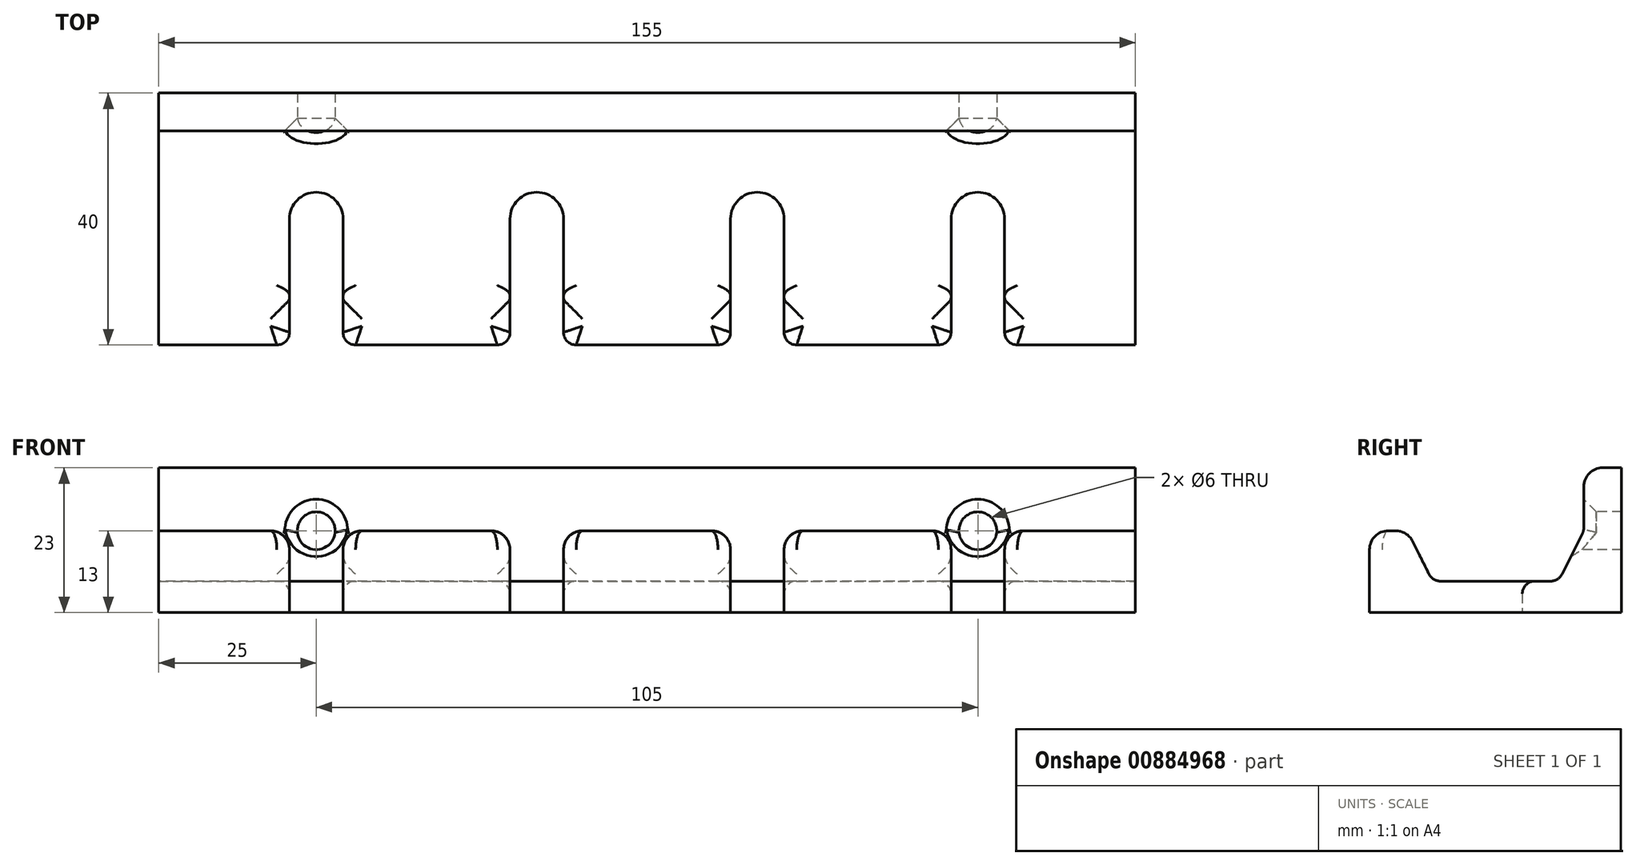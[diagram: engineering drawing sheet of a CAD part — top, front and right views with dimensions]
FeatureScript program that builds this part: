
annotation { "Feature Type Name" : "Feature", "Feature Type Description" : "" }
export const myFeature = defineFeature(function(context is Context, id is Id, definition is map)
    precondition{}
    {
        {
            var Q0;
            Q0=qCreatedBy(makeId("Top.planeOp"),FACE);
            var sketch = newSketch(context, id + "F0", { "sketchPlane" : qUnion([Q0])});
            skLineSegment(sketch, "E0.bottom", {"start": v(-77.5, 20) * mm, "end": v(77.5, 20) * mm});
            skLineSegment(sketch, "E0.top", {"start": v(-77.5, -20) * mm, "end": v(77.5, -20) * mm});
            skLineSegment(sketch, "E0.left", {"start": v(-77.5, 20) * mm, "end": v(-77.5, -20) * mm});
            skLineSegment(sketch, "E0.right", {"start": v(77.5, 20) * mm, "end": v(77.5, -20) * mm});
            skPoint(sketch, "E0.middle", {"position": v(0, 0) * mm});
            skSolve(sketch);
        }
        {
            var Q0;
            Q0=makeQuery(id+"F0.imprint","IMPRINT",FACE,{"disambiguationData":[TD([[makeQuery(id+"F0.imprint","IMPRINT",EDGE,{"derivedFrom":sQuery(id+"F0.wireOp",EDGE,"E0.bottom")}),-1.0]])]});
            extrude(context, id + "F1", {"entities" : qUnion([Q0]), "depth" : 5 * mm, "offsetDistance" : 25 * mm});
        }
        {
            var Q0;
            Q0=makeQuery(id+"F1.opExtrude","CAP_FACE",FACE,{"disambiguationData":[OSD([sQuery(id+"F0.wireOp",EDGE,"E0.bottom"),sQuery(id+"F0.wireOp",EDGE,"E0.top"),sQuery(id+"F0.wireOp",EDGE,"E0.left"),sQuery(id+"F0.wireOp",EDGE,"E0.right")])],"isStart":false});
            var sketch = newSketch(context, id + "F2", { "sketchPlane" : qUnion([Q0])});
            skLineSegment(sketch, "E1.bottom", {"start": v(-77.5, 10) * mm, "end": v(77.5, 10) * mm});
            skLineSegment(sketch, "E1.top", {"start": v(-77.5, -10) * mm, "end": v(77.5, -10) * mm});
            skLineSegment(sketch, "E1.left", {"start": v(-77.5, 10) * mm, "end": v(-77.5, -10) * mm});
            skLineSegment(sketch, "E1.right", {"start": v(77.5, 10) * mm, "end": v(77.5, -10) * mm});
            skPoint(sketch, "E1.middle", {"position": v(0, 0) * mm});
            skLineSegment(sketch, "E2.bottom", {"start": v(-77.5, 20) * mm, "end": v(77.5, 20) * mm});
            skLineSegment(sketch, "E2.top", {"start": v(-77.5, -20) * mm, "end": v(77.5, -20) * mm});
            skLineSegment(sketch, "E2.left", {"start": v(-77.5, 20) * mm, "end": v(-77.5, -20) * mm});
            skLineSegment(sketch, "E2.right", {"start": v(77.5, 20) * mm, "end": v(77.5, -20) * mm});
            skSolve(sketch);
        }
        {
            var Q0;
            {var subQ0=sQuery(id+"F2.wireOp",EDGE,"E1.bottom");Q0=makeQuery(id+"F2.imprint","IMPRINT",FACE,{"disambiguationData":[TD([[makeQuery(id+"F2.imprint","IMPRINT",EDGE,{"derivedFrom":subQ0}),1.0]])]});}
            var Q1;
            {var subQ0=sQuery(id+"F2.wireOp",EDGE,"E1.top");Q1=makeQuery(id+"F2.imprint","IMPRINT",FACE,{"disambiguationData":[TD([[makeQuery(id+"F2.imprint","IMPRINT",EDGE,{"derivedFrom":subQ0}),-1.0]])]});}
            extrude(context, id + "F3", {"entities" : qUnion([Q0, Q1]), "operationType" : NewBodyOperationType.ADD, "depth" : 8 * mm, "offsetDistance" : 25 * mm});
        }
        {
            var Q0;
            Q0=makeQuery(id+"F3.opExtrude","CAP_EDGE",EDGE,{"disambiguationData":[OSD([sQuery(id+"F2.wireOp",EDGE,"E1.bottom")])],"isStart":false});
            chamfer(context, id + "F4", {"entities" : qUnion([Q0]), "chamferType" : ChamferType.TWO_OFFSETS, "width1" : 8 * mm, "oppositeDirection" : true, "width2" : 4 * mm});
        }
        {
            var Q0;
            Q0=makeQuery(id+"F3.opExtrude","CAP_EDGE",EDGE,{"disambiguationData":[OSD([sQuery(id+"F2.wireOp",EDGE,"E1.top")])],"isStart":false});
            chamfer(context, id + "F5", {"entities" : qUnion([Q0]), "chamferType" : ChamferType.TWO_OFFSETS, "width1" : 8 * mm, "oppositeDirection" : false, "width2" : 4 * mm, "tangentPropagation" : true});
        }
        {
            var Q0;
            Q0=makeQuery(id+"F0.imprint","IMPRINT",FACE,{"disambiguationData":[TD([[makeQuery(id+"F0.imprint","IMPRINT",EDGE,{"derivedFrom":sQuery(id+"F0.wireOp",EDGE,"E0.bottom")}),-1.0]])]});
            var sketch = newSketch(context, id + "F6", { "sketchPlane" : qUnion([Q0])});
            skCircle(sketch, "E3", {"center": v(-52.5, 0) * mm, "radius": 4.25 * mm});
            skCircle(sketch, "E4.1.0.0", {"center": v(-17.5, 0) * mm, "radius": 4.25 * mm});
            skCircle(sketch, "E4.2.0.0", {"center": v(17.5, 0) * mm, "radius": 4.25 * mm});
            skCircle(sketch, "E4.3.0.0", {"center": v(52.5, 0) * mm, "radius": 4.25 * mm});
            skLineSegment(sketch, "E4.direction1", {"start": v(-52.5, 0) * mm, "end": v(-17.5, 0) * mm, "construction": true});
            skLineSegment(sketch, "E5", {"start": v(-48.25, 0) * mm, "end": v(-48.25, -25) * mm});
            skLineSegment(sketch, "E6", {"start": v(-56.75, 0) * mm, "end": v(-56.75, -25) * mm});
            skLineSegment(sketch, "E7", {"start": v(-21.75, 0) * mm, "end": v(-21.75, -25) * mm});
            skLineSegment(sketch, "E8", {"start": v(-80.14, 0) * mm, "end": v(82.26, 0) * mm, "construction": true});
            skLineSegment(sketch, "E9", {"start": v(-13.25, 0) * mm, "end": v(-13.25, -25) * mm});
            skLineSegment(sketch, "E10", {"start": v(13.25, 0) * mm, "end": v(13.25, -25) * mm});
            skLineSegment(sketch, "E11", {"start": v(21.75, 0) * mm, "end": v(21.75, -25) * mm});
            skLineSegment(sketch, "E12", {"start": v(48.25, 0) * mm, "end": v(48.25, -25) * mm});
            skLineSegment(sketch, "E13", {"start": v(56.75, 0) * mm, "end": v(56.75, -25) * mm});
            skLineSegment(sketch, "E14", {"start": v(-48.25, -25) * mm, "end": v(-56.75, -25) * mm});
            skLineSegment(sketch, "E15", {"start": v(-21.75, -25) * mm, "end": v(-13.25, -25) * mm});
            skLineSegment(sketch, "E16", {"start": v(13.25, -25) * mm, "end": v(21.75, -25) * mm});
            skLineSegment(sketch, "E17", {"start": v(48.25, -25) * mm, "end": v(56.75, -25) * mm});
            skSolve(sketch);
        }
        {
            var Q0;
            Q0 = qSketchRegion(id + "F6", true);
            extrude(context, id + "F7", {"entities" : qUnion([Q0]), "operationType" : NewBodyOperationType.REMOVE, "depth" : 25 * mm, "offsetDistance" : 25 * mm});
        }
        {
            var Q0;
            Q0=makeQuery(id+"F3.opExtrude","CAP_FACE",FACE,{"disambiguationData":[OSD([sQuery(id+"F2.wireOp",EDGE,"E1.bottom"),sQuery(id+"F2.wireOp",EDGE,"E2.bottom"),sQuery(id+"F2.wireOp",EDGE,"E2.left"),sQuery(id+"F2.wireOp",EDGE,"E2.right")])],"isStart":false});
            extrude(context, id + "F8", {"entities" : qUnion([Q0]), "operationType" : NewBodyOperationType.ADD, "depth" : 10 * mm, "offsetDistance" : 25 * mm});
        }
        {
            var Q0;
            Q0=makeQuery(id+"F8.opExtrude","SWEPT_FACE",FACE,{"disambiguationData":[OSD([sQuery(id+"F2.wireOp",EDGE,"E1.bottom"),sQuery(id+"F2.wireOp",EDGE,"E2.bottom"),sQuery(id+"F2.wireOp",EDGE,"E2.left"),sQuery(id+"F2.wireOp",EDGE,"E2.right")])]});
            var sketch = newSketch(context, id + "F9", { "sketchPlane" : qUnion([Q0])});
            skCircle(sketch, "E18", {"center": v(-52.5, 13) * mm, "radius": 3 * mm});
            skCircle(sketch, "E19", {"center": v(52.5, 13) * mm, "radius": 3 * mm});
            skSolve(sketch);
        }
        {
            var Q0;
            Q0 = qSketchRegion(id + "F9", true);
            extrude(context, id + "F10", {"entities" : qUnion([Q0]), "operationType" : NewBodyOperationType.REMOVE, "oppositeDirection" : true, "depth" : 15 * mm, "offsetDistance" : 25 * mm, "hasSecondDirection" : true, "secondDirectionOppositeDirection" : false, "secondDirectionDepth" : 15 * mm});
        }
        {
            var Q0;
            Q0=makeQuery(id+"F10.boolean.opBoolean","INTERSECT",EDGE,{"derivedFrom":[makeQuery(id+"F4.opChamfer","BLEND_FACE",FACE,{"disambiguationData":[OSD([sQuery(id+"F2.wireOp",EDGE,"E1.bottom")])]}),makeQuery(id+"F10.opExtrude","SWEPT_FACE",FACE,{"disambiguationData":[OSD([sQuery(id+"F9.wireOp",EDGE,"E18")])]})]});
            var Q1;
            Q1=makeQuery(id+"F10.boolean.opBoolean","INTERSECT",EDGE,{"derivedFrom":[makeQuery(id+"F8.opExtrude","SWEPT_FACE",FACE,{"disambiguationData":[OSD([sQuery(id+"F2.wireOp",EDGE,"E1.bottom"),sQuery(id+"F2.wireOp",EDGE,"E2.bottom"),sQuery(id+"F2.wireOp",EDGE,"E2.left"),sQuery(id+"F2.wireOp",EDGE,"E2.right")])]}),makeQuery(id+"F10.opExtrude","SWEPT_FACE",FACE,{"disambiguationData":[OSD([sQuery(id+"F9.wireOp",EDGE,"E18")])]})]});
            var Q2;
            Q2=makeQuery(id+"F10.boolean.opBoolean","INTERSECT",EDGE,{"derivedFrom":[makeQuery(id+"F4.opChamfer","BLEND_FACE",FACE,{"disambiguationData":[OSD([sQuery(id+"F2.wireOp",EDGE,"E1.bottom")])]}),makeQuery(id+"F10.opExtrude","SWEPT_FACE",FACE,{"disambiguationData":[OSD([sQuery(id+"F9.wireOp",EDGE,"E19")])]})]});
            var Q3;
            Q3=makeQuery(id+"F10.boolean.opBoolean","INTERSECT",EDGE,{"derivedFrom":[makeQuery(id+"F8.opExtrude","SWEPT_FACE",FACE,{"disambiguationData":[OSD([sQuery(id+"F2.wireOp",EDGE,"E1.bottom"),sQuery(id+"F2.wireOp",EDGE,"E2.bottom"),sQuery(id+"F2.wireOp",EDGE,"E2.left"),sQuery(id+"F2.wireOp",EDGE,"E2.right")])]}),makeQuery(id+"F10.opExtrude","SWEPT_FACE",FACE,{"disambiguationData":[OSD([sQuery(id+"F9.wireOp",EDGE,"E19")])]})]});
            chamfer(context, id + "F11", {"entities" : qUnion([Q0, Q1, Q2, Q3]), "width" : 2 * mm, "tangentPropagation" : true});
        }
        {
            var Q0;
            Q0=makeQuery(id+"F7.boolean.opBoolean","INTERSECT",EDGE,{"derivedFrom":[makeQuery(id+"F1.opExtrude","CAP_FACE",FACE,{"disambiguationData":[OSD([sQuery(id+"F0.wireOp",EDGE,"E0.bottom"),sQuery(id+"F0.wireOp",EDGE,"E0.top"),sQuery(id+"F0.wireOp",EDGE,"E0.left"),sQuery(id+"F0.wireOp",EDGE,"E0.right")])],"isStart":false}),makeQuery(id+"F7.opExtrude","SWEPT_FACE",FACE,{"disambiguationData":[OSD([sQuery(id+"F6.wireOp",EDGE,"E6")])]})]});
            var Q1;
            Q1=makeQuery(id+"F7.boolean.opBoolean","INTERSECT",EDGE,{"derivedFrom":[makeQuery(id+"F1.opExtrude","CAP_FACE",FACE,{"disambiguationData":[OSD([sQuery(id+"F0.wireOp",EDGE,"E0.bottom"),sQuery(id+"F0.wireOp",EDGE,"E0.top"),sQuery(id+"F0.wireOp",EDGE,"E0.left"),sQuery(id+"F0.wireOp",EDGE,"E0.right")])],"isStart":false}),makeQuery(id+"F7.opExtrude","SWEPT_FACE",FACE,{"disambiguationData":[OSD([sQuery(id+"F6.wireOp",EDGE,"E3")])]})]});
            var Q2;
            Q2=makeQuery(id+"F7.boolean.opBoolean","INTERSECT",EDGE,{"derivedFrom":[makeQuery(id+"F1.opExtrude","CAP_FACE",FACE,{"disambiguationData":[OSD([sQuery(id+"F0.wireOp",EDGE,"E0.bottom"),sQuery(id+"F0.wireOp",EDGE,"E0.top"),sQuery(id+"F0.wireOp",EDGE,"E0.left"),sQuery(id+"F0.wireOp",EDGE,"E0.right")])],"isStart":false}),makeQuery(id+"F7.opExtrude","SWEPT_FACE",FACE,{"disambiguationData":[OSD([sQuery(id+"F6.wireOp",EDGE,"E5")])]})]});
            var Q3;
            Q3=makeQuery(id+"F7.boolean.opBoolean","INTERSECT",EDGE,{"derivedFrom":[makeQuery(id+"F1.opExtrude","CAP_FACE",FACE,{"disambiguationData":[OSD([sQuery(id+"F0.wireOp",EDGE,"E0.bottom"),sQuery(id+"F0.wireOp",EDGE,"E0.top"),sQuery(id+"F0.wireOp",EDGE,"E0.left"),sQuery(id+"F0.wireOp",EDGE,"E0.right")])],"isStart":false}),makeQuery(id+"F7.opExtrude","SWEPT_FACE",FACE,{"disambiguationData":[OSD([sQuery(id+"F6.wireOp",EDGE,"E7")])]})]});
            var Q4;
            Q4=makeQuery(id+"F7.boolean.opBoolean","INTERSECT",EDGE,{"derivedFrom":[makeQuery(id+"F1.opExtrude","CAP_FACE",FACE,{"disambiguationData":[OSD([sQuery(id+"F0.wireOp",EDGE,"E0.bottom"),sQuery(id+"F0.wireOp",EDGE,"E0.top"),sQuery(id+"F0.wireOp",EDGE,"E0.left"),sQuery(id+"F0.wireOp",EDGE,"E0.right")])],"isStart":false}),makeQuery(id+"F7.opExtrude","SWEPT_FACE",FACE,{"disambiguationData":[OSD([sQuery(id+"F6.wireOp",EDGE,"E4.1.0.0")])]})]});
            var Q5;
            Q5=makeQuery(id+"F7.boolean.opBoolean","INTERSECT",EDGE,{"derivedFrom":[makeQuery(id+"F1.opExtrude","CAP_FACE",FACE,{"disambiguationData":[OSD([sQuery(id+"F0.wireOp",EDGE,"E0.bottom"),sQuery(id+"F0.wireOp",EDGE,"E0.top"),sQuery(id+"F0.wireOp",EDGE,"E0.left"),sQuery(id+"F0.wireOp",EDGE,"E0.right")])],"isStart":false}),makeQuery(id+"F7.opExtrude","SWEPT_FACE",FACE,{"disambiguationData":[OSD([sQuery(id+"F6.wireOp",EDGE,"E9")])]})]});
            var Q6;
            Q6=makeQuery(id+"F7.boolean.opBoolean","INTERSECT",EDGE,{"derivedFrom":[makeQuery(id+"F1.opExtrude","CAP_FACE",FACE,{"disambiguationData":[OSD([sQuery(id+"F0.wireOp",EDGE,"E0.bottom"),sQuery(id+"F0.wireOp",EDGE,"E0.top"),sQuery(id+"F0.wireOp",EDGE,"E0.left"),sQuery(id+"F0.wireOp",EDGE,"E0.right")])],"isStart":false}),makeQuery(id+"F7.opExtrude","SWEPT_FACE",FACE,{"disambiguationData":[OSD([sQuery(id+"F6.wireOp",EDGE,"E10")])]})]});
            var Q7;
            Q7=makeQuery(id+"F7.boolean.opBoolean","INTERSECT",EDGE,{"derivedFrom":[makeQuery(id+"F1.opExtrude","CAP_FACE",FACE,{"disambiguationData":[OSD([sQuery(id+"F0.wireOp",EDGE,"E0.bottom"),sQuery(id+"F0.wireOp",EDGE,"E0.top"),sQuery(id+"F0.wireOp",EDGE,"E0.left"),sQuery(id+"F0.wireOp",EDGE,"E0.right")])],"isStart":false}),makeQuery(id+"F7.opExtrude","SWEPT_FACE",FACE,{"disambiguationData":[OSD([sQuery(id+"F6.wireOp",EDGE,"E12")])]})]});
            var Q8;
            Q8=makeQuery(id+"F7.boolean.opBoolean","COPY",EDGE,{"derivedFrom":makeQuery(id+"F7.opExtrude","CAP_EDGE",EDGE,{"disambiguationData":[OSD([sQuery(id+"F6.wireOp",EDGE,"E5")])],"isStart":true})});
            var Q9;
            Q9=makeQuery(id+"F7.boolean.opBoolean","COPY",EDGE,{"derivedFrom":makeQuery(id+"F7.opExtrude","CAP_EDGE",EDGE,{"disambiguationData":[OSD([sQuery(id+"F6.wireOp",EDGE,"E9")])],"isStart":true})});
            var Q10;
            Q10=makeQuery(id+"F7.boolean.opBoolean","COPY",EDGE,{"derivedFrom":makeQuery(id+"F7.opExtrude","CAP_EDGE",EDGE,{"disambiguationData":[OSD([sQuery(id+"F6.wireOp",EDGE,"E11")])],"isStart":true})});
            var Q11;
            Q11=makeQuery(id+"F7.boolean.opBoolean","COPY",EDGE,{"derivedFrom":makeQuery(id+"F7.opExtrude","CAP_EDGE",EDGE,{"disambiguationData":[OSD([sQuery(id+"F6.wireOp",EDGE,"E13")])],"isStart":true})});
            var Q12;
            Q12=makeQuery(id+"F7.boolean.opBoolean","INTERSECT",EDGE,{"derivedFrom":[makeQuery(id+"F3.boolean.opBoolean","MERGE",FACE,{"derivedFrom":[makeQuery(id+"F1.opExtrude","SWEPT_FACE",FACE,{"disambiguationData":[OSD([sQuery(id+"F0.wireOp",EDGE,"E0.top")])]}),makeQuery(id+"F3.opExtrude","SWEPT_FACE",FACE,{"disambiguationData":[OSD([sQuery(id+"F2.wireOp",EDGE,"E2.top")])]})]}),makeQuery(id+"F7.opExtrude","SWEPT_FACE",FACE,{"disambiguationData":[OSD([sQuery(id+"F6.wireOp",EDGE,"E6")])]})]});
            var Q13;
            Q13=makeQuery(id+"F7.boolean.opBoolean","INTERSECT",EDGE,{"derivedFrom":[makeQuery(id+"F3.boolean.opBoolean","MERGE",FACE,{"derivedFrom":[makeQuery(id+"F1.opExtrude","SWEPT_FACE",FACE,{"disambiguationData":[OSD([sQuery(id+"F0.wireOp",EDGE,"E0.top")])]}),makeQuery(id+"F3.opExtrude","SWEPT_FACE",FACE,{"disambiguationData":[OSD([sQuery(id+"F2.wireOp",EDGE,"E2.top")])]})]}),makeQuery(id+"F7.opExtrude","SWEPT_FACE",FACE,{"disambiguationData":[OSD([sQuery(id+"F6.wireOp",EDGE,"E5")])]})]});
            var Q14;
            Q14=makeQuery(id+"F7.boolean.opBoolean","INTERSECT",EDGE,{"derivedFrom":[makeQuery(id+"F3.boolean.opBoolean","MERGE",FACE,{"derivedFrom":[makeQuery(id+"F1.opExtrude","SWEPT_FACE",FACE,{"disambiguationData":[OSD([sQuery(id+"F0.wireOp",EDGE,"E0.top")])]}),makeQuery(id+"F3.opExtrude","SWEPT_FACE",FACE,{"disambiguationData":[OSD([sQuery(id+"F2.wireOp",EDGE,"E2.top")])]})]}),makeQuery(id+"F7.opExtrude","SWEPT_FACE",FACE,{"disambiguationData":[OSD([sQuery(id+"F6.wireOp",EDGE,"E7")])]})]});
            var Q15;
            Q15=makeQuery(id+"F7.boolean.opBoolean","INTERSECT",EDGE,{"derivedFrom":[makeQuery(id+"F3.boolean.opBoolean","MERGE",FACE,{"derivedFrom":[makeQuery(id+"F1.opExtrude","SWEPT_FACE",FACE,{"disambiguationData":[OSD([sQuery(id+"F0.wireOp",EDGE,"E0.top")])]}),makeQuery(id+"F3.opExtrude","SWEPT_FACE",FACE,{"disambiguationData":[OSD([sQuery(id+"F2.wireOp",EDGE,"E2.top")])]})]}),makeQuery(id+"F7.opExtrude","SWEPT_FACE",FACE,{"disambiguationData":[OSD([sQuery(id+"F6.wireOp",EDGE,"E9")])]})]});
            var Q16;
            Q16=makeQuery(id+"F7.boolean.opBoolean","INTERSECT",EDGE,{"derivedFrom":[makeQuery(id+"F3.boolean.opBoolean","MERGE",FACE,{"derivedFrom":[makeQuery(id+"F1.opExtrude","SWEPT_FACE",FACE,{"disambiguationData":[OSD([sQuery(id+"F0.wireOp",EDGE,"E0.top")])]}),makeQuery(id+"F3.opExtrude","SWEPT_FACE",FACE,{"disambiguationData":[OSD([sQuery(id+"F2.wireOp",EDGE,"E2.top")])]})]}),makeQuery(id+"F7.opExtrude","SWEPT_FACE",FACE,{"disambiguationData":[OSD([sQuery(id+"F6.wireOp",EDGE,"E10")])]})]});
            var Q17;
            Q17=makeQuery(id+"F7.boolean.opBoolean","INTERSECT",EDGE,{"derivedFrom":[makeQuery(id+"F3.boolean.opBoolean","MERGE",FACE,{"derivedFrom":[makeQuery(id+"F1.opExtrude","SWEPT_FACE",FACE,{"disambiguationData":[OSD([sQuery(id+"F0.wireOp",EDGE,"E0.top")])]}),makeQuery(id+"F3.opExtrude","SWEPT_FACE",FACE,{"disambiguationData":[OSD([sQuery(id+"F2.wireOp",EDGE,"E2.top")])]})]}),makeQuery(id+"F7.opExtrude","SWEPT_FACE",FACE,{"disambiguationData":[OSD([sQuery(id+"F6.wireOp",EDGE,"E11")])]})]});
            var Q18;
            Q18=makeQuery(id+"F7.boolean.opBoolean","INTERSECT",EDGE,{"derivedFrom":[makeQuery(id+"F3.boolean.opBoolean","MERGE",FACE,{"derivedFrom":[makeQuery(id+"F1.opExtrude","SWEPT_FACE",FACE,{"disambiguationData":[OSD([sQuery(id+"F0.wireOp",EDGE,"E0.top")])]}),makeQuery(id+"F3.opExtrude","SWEPT_FACE",FACE,{"disambiguationData":[OSD([sQuery(id+"F2.wireOp",EDGE,"E2.top")])]})]}),makeQuery(id+"F7.opExtrude","SWEPT_FACE",FACE,{"disambiguationData":[OSD([sQuery(id+"F6.wireOp",EDGE,"E12")])]})]});
            var Q19;
            Q19=makeQuery(id+"F7.boolean.opBoolean","INTERSECT",EDGE,{"derivedFrom":[makeQuery(id+"F3.boolean.opBoolean","MERGE",FACE,{"derivedFrom":[makeQuery(id+"F1.opExtrude","SWEPT_FACE",FACE,{"disambiguationData":[OSD([sQuery(id+"F0.wireOp",EDGE,"E0.top")])]}),makeQuery(id+"F3.opExtrude","SWEPT_FACE",FACE,{"disambiguationData":[OSD([sQuery(id+"F2.wireOp",EDGE,"E2.top")])]})]}),makeQuery(id+"F7.opExtrude","SWEPT_FACE",FACE,{"disambiguationData":[OSD([sQuery(id+"F6.wireOp",EDGE,"E13")])]})]});
            var Q20;
            {var subQ0=makeQuery(id+"F1.opExtrude","CAP_FACE",FACE,{"disambiguationData":[OSD([sQuery(id+"F0.wireOp",EDGE,"E0.bottom"),sQuery(id+"F0.wireOp",EDGE,"E0.top"),sQuery(id+"F0.wireOp",EDGE,"E0.left"),sQuery(id+"F0.wireOp",EDGE,"E0.right")])],"isStart":false});var subQ1=sQuery(id+"F2.wireOp",EDGE,"E1.top");Q20=makeQuery(id+"F7.boolean.opBoolean","SPLIT",EDGE,{"disambiguationData":[TD([makeQuery(id+"F7.opExtrude","SWEPT_FACE",FACE,{"disambiguationData":[OSD([sQuery(id+"F6.wireOp",EDGE,"E9")])]})])],"derivedFrom":makeQuery(id+"F5.opChamfer","BLEND_EDGE",EDGE,{"blendedFrom":[makeQuery(id+"F3.opExtrude","CAP_EDGE",EDGE,{"disambiguationData":[OSD([subQ1])],"isStart":false}),subQ0],"blendedInto":[subQ0]})});}
            var Q21;
            {var subQ0=makeQuery(id+"F1.opExtrude","CAP_FACE",FACE,{"disambiguationData":[OSD([sQuery(id+"F0.wireOp",EDGE,"E0.bottom"),sQuery(id+"F0.wireOp",EDGE,"E0.top"),sQuery(id+"F0.wireOp",EDGE,"E0.left"),sQuery(id+"F0.wireOp",EDGE,"E0.right")])],"isStart":false});var subQ1=sQuery(id+"F2.wireOp",EDGE,"E1.top");Q21=makeQuery(id+"F7.boolean.opBoolean","SPLIT",EDGE,{"disambiguationData":[TD([makeQuery(id+"F7.opExtrude","SWEPT_FACE",FACE,{"disambiguationData":[OSD([sQuery(id+"F6.wireOp",EDGE,"E5")])]})])],"derivedFrom":makeQuery(id+"F5.opChamfer","BLEND_EDGE",EDGE,{"blendedFrom":[makeQuery(id+"F3.opExtrude","CAP_EDGE",EDGE,{"disambiguationData":[OSD([subQ1])],"isStart":false}),subQ0],"blendedInto":[subQ0]})});}
            var Q22;
            {var subQ1=sQuery(id+"F0.wireOp",EDGE,"E0.left");var subQ2=sQuery(id+"F2.wireOp",EDGE,"E1.top");var subQ3=makeQuery(id+"F1.opExtrude","CAP_FACE",FACE,{"disambiguationData":[OSD([sQuery(id+"F0.wireOp",EDGE,"E0.bottom"),sQuery(id+"F0.wireOp",EDGE,"E0.top"),subQ1,sQuery(id+"F0.wireOp",EDGE,"E0.right")])],"isStart":false});Q22=makeQuery(id+"F7.boolean.opBoolean","SPLIT",EDGE,{"disambiguationData":[TD([makeQuery(id+"F1.opExtrude","SWEPT_FACE",FACE,{"disambiguationData":[OSD([subQ1])]})])],"derivedFrom":makeQuery(id+"F5.opChamfer","BLEND_EDGE",EDGE,{"blendedFrom":[makeQuery(id+"F3.opExtrude","CAP_EDGE",EDGE,{"disambiguationData":[OSD([subQ2])],"isStart":false}),subQ3],"blendedInto":[subQ3]})});}
            var Q23;
            {var subQ0=makeQuery(id+"F1.opExtrude","CAP_FACE",FACE,{"disambiguationData":[OSD([sQuery(id+"F0.wireOp",EDGE,"E0.bottom"),sQuery(id+"F0.wireOp",EDGE,"E0.top"),sQuery(id+"F0.wireOp",EDGE,"E0.left"),sQuery(id+"F0.wireOp",EDGE,"E0.right")])],"isStart":false});var subQ1=sQuery(id+"F2.wireOp",EDGE,"E1.top");Q23=makeQuery(id+"F7.boolean.opBoolean","SPLIT",EDGE,{"disambiguationData":[TD([makeQuery(id+"F7.opExtrude","SWEPT_FACE",FACE,{"disambiguationData":[OSD([sQuery(id+"F6.wireOp",EDGE,"E11")])]})])],"derivedFrom":makeQuery(id+"F5.opChamfer","BLEND_EDGE",EDGE,{"blendedFrom":[makeQuery(id+"F3.opExtrude","CAP_EDGE",EDGE,{"disambiguationData":[OSD([subQ1])],"isStart":false}),subQ0],"blendedInto":[subQ0]})});}
            var Q24;
            {var subQ1=sQuery(id+"F2.wireOp",EDGE,"E1.top");var subQ2=sQuery(id+"F0.wireOp",EDGE,"E0.right");var subQ3=makeQuery(id+"F1.opExtrude","CAP_FACE",FACE,{"disambiguationData":[OSD([sQuery(id+"F0.wireOp",EDGE,"E0.bottom"),sQuery(id+"F0.wireOp",EDGE,"E0.top"),sQuery(id+"F0.wireOp",EDGE,"E0.left"),subQ2])],"isStart":false});Q24=makeQuery(id+"F7.boolean.opBoolean","SPLIT",EDGE,{"disambiguationData":[TD([makeQuery(id+"F1.opExtrude","SWEPT_FACE",FACE,{"disambiguationData":[OSD([subQ2])]})])],"derivedFrom":makeQuery(id+"F5.opChamfer","BLEND_EDGE",EDGE,{"blendedFrom":[makeQuery(id+"F3.opExtrude","CAP_EDGE",EDGE,{"disambiguationData":[OSD([subQ1])],"isStart":false}),subQ3],"blendedInto":[subQ3]})});}
            var Q25;
            Q25=makeQuery(id+"F4.opChamfer","BLEND_EDGE",EDGE,{"blendedFrom":[makeQuery(id+"F3.opExtrude","CAP_EDGE",EDGE,{"disambiguationData":[OSD([sQuery(id+"F2.wireOp",EDGE,"E1.bottom")])],"isStart":false}),makeQuery(id+"F1.opExtrude","CAP_FACE",FACE,{"disambiguationData":[OSD([sQuery(id+"F0.wireOp",EDGE,"E0.bottom"),sQuery(id+"F0.wireOp",EDGE,"E0.top"),sQuery(id+"F0.wireOp",EDGE,"E0.left"),sQuery(id+"F0.wireOp",EDGE,"E0.right")])],"isStart":false})],"blendedInto":[makeQuery(id+"F1.opExtrude","CAP_FACE",FACE,{"disambiguationData":[OSD([sQuery(id+"F0.wireOp",EDGE,"E0.bottom"),sQuery(id+"F0.wireOp",EDGE,"E0.top"),sQuery(id+"F0.wireOp",EDGE,"E0.left"),sQuery(id+"F0.wireOp",EDGE,"E0.right")])],"isStart":false})]});
            var Q26;
            {var subQ0=sQuery(id+"F2.wireOp",EDGE,"E1.bottom");var subQ1=sQuery(id+"F2.wireOp",EDGE,"E2.left");var subQ2=sQuery(id+"F2.wireOp",EDGE,"E2.bottom");var subQ3=sQuery(id+"F2.wireOp",EDGE,"E2.right");Q26=makeQuery(id+"F10.boolean.opBoolean","SPLIT",EDGE,{"disambiguationData":[TD([makeQuery(id+"F1.opExtrude","SWEPT_FACE",FACE,{"disambiguationData":[OSD([sQuery(id+"F0.wireOp",EDGE,"E0.left")])]}),makeQuery(id+"F3.opExtrude","SWEPT_FACE",FACE,{"disambiguationData":[OSD([subQ1]),TDD([makeQuery(id+"F2.imprint","IMPRINT",EDGE,{"disambiguationData":[TD([[makeQuery(id+"F2.imprint","INTERSECT",VERTEX,{"derivedFrom":[subQ2,subQ1]}),-1.0]])],"derivedFrom":subQ1})])]}),makeQuery(id+"F3.opExtrude","SWEPT_FACE",FACE,{"disambiguationData":[OSD([subQ1]),TDD([makeQuery(id+"F2.imprint","IMPRINT",EDGE,{"disambiguationData":[TD([[makeQuery(id+"F2.imprint","INTERSECT",VERTEX,{"derivedFrom":[sQuery(id+"F2.wireOp",EDGE,"E2.top"),subQ1]}),1.0]])],"derivedFrom":subQ1})])]}),makeQuery(id+"F4.opChamfer","BLEND_FACE",FACE,{"disambiguationData":[OSD([subQ0])]}),makeQuery(id+"F8.opExtrude","SWEPT_FACE",FACE,{"disambiguationData":[OSD([subQ0,subQ2,subQ1,subQ3])]}),makeQuery(id+"F8.opExtrude","SWEPT_FACE",FACE,{"disambiguationData":[OSD([subQ1])]}),makeQuery(id+"F10.opExtrude","SWEPT_FACE",FACE,{"disambiguationData":[OSD([sQuery(id+"F9.wireOp",EDGE,"E18")])]})])],"derivedFrom":makeQuery(id+"F8.boolean.opBoolean","MERGE",EDGE,{"derivedFrom":[makeQuery(id+"F4.opChamfer","BLEND_EDGE",EDGE,{"blendedFrom":[makeQuery(id+"F3.opExtrude","CAP_EDGE",EDGE,{"disambiguationData":[OSD([subQ0])],"isStart":false}),makeQuery(id+"F3.opExtrude","CAP_FACE",FACE,{"disambiguationData":[OSD([subQ0,subQ2,subQ1,subQ3])],"isStart":false})],"blendedInto":[makeQuery(id+"F3.opExtrude","CAP_FACE",FACE,{"disambiguationData":[OSD([subQ0,subQ2,subQ1,subQ3])],"isStart":false})]}),makeQuery(id+"F8.opExtrude","CAP_EDGE",EDGE,{"disambiguationData":[OSD([subQ0,subQ2,subQ1,subQ3])],"isStart":true})]})});}
            var Q27;
            {var subQ0=sQuery(id+"F2.wireOp",EDGE,"E1.bottom");var subQ1=sQuery(id+"F2.wireOp",EDGE,"E2.right");var subQ2=sQuery(id+"F2.wireOp",EDGE,"E2.left");var subQ3=sQuery(id+"F2.wireOp",EDGE,"E2.bottom");Q27=makeQuery(id+"F10.boolean.opBoolean","SPLIT",EDGE,{"disambiguationData":[TD([makeQuery(id+"F4.opChamfer","BLEND_FACE",FACE,{"disambiguationData":[OSD([subQ0])]}),makeQuery(id+"F8.opExtrude","SWEPT_FACE",FACE,{"disambiguationData":[OSD([subQ0,subQ3,subQ2,subQ1])]}),makeQuery(id+"F10.opExtrude","SWEPT_FACE",FACE,{"disambiguationData":[OSD([sQuery(id+"F9.wireOp",EDGE,"E18")])]}),makeQuery(id+"F10.opExtrude","SWEPT_FACE",FACE,{"disambiguationData":[OSD([sQuery(id+"F9.wireOp",EDGE,"E19")])]})])],"derivedFrom":makeQuery(id+"F8.boolean.opBoolean","MERGE",EDGE,{"derivedFrom":[makeQuery(id+"F4.opChamfer","BLEND_EDGE",EDGE,{"blendedFrom":[makeQuery(id+"F3.opExtrude","CAP_EDGE",EDGE,{"disambiguationData":[OSD([subQ0])],"isStart":false}),makeQuery(id+"F3.opExtrude","CAP_FACE",FACE,{"disambiguationData":[OSD([subQ0,subQ3,subQ2,subQ1])],"isStart":false})],"blendedInto":[makeQuery(id+"F3.opExtrude","CAP_FACE",FACE,{"disambiguationData":[OSD([subQ0,subQ3,subQ2,subQ1])],"isStart":false})]}),makeQuery(id+"F8.opExtrude","CAP_EDGE",EDGE,{"disambiguationData":[OSD([subQ0,subQ3,subQ2,subQ1])],"isStart":true})]})});}
            var Q28;
            {var subQ0=sQuery(id+"F2.wireOp",EDGE,"E2.right");var subQ1=sQuery(id+"F2.wireOp",EDGE,"E2.bottom");var subQ2=sQuery(id+"F2.wireOp",EDGE,"E1.bottom");var subQ3=sQuery(id+"F2.wireOp",EDGE,"E2.left");Q28=makeQuery(id+"F10.boolean.opBoolean","SPLIT",EDGE,{"disambiguationData":[TD([makeQuery(id+"F1.opExtrude","SWEPT_FACE",FACE,{"disambiguationData":[OSD([sQuery(id+"F0.wireOp",EDGE,"E0.right")])]}),makeQuery(id+"F3.opExtrude","SWEPT_FACE",FACE,{"disambiguationData":[OSD([subQ0]),TDD([makeQuery(id+"F2.imprint","IMPRINT",EDGE,{"disambiguationData":[TD([[makeQuery(id+"F2.imprint","INTERSECT",VERTEX,{"derivedFrom":[subQ1,subQ0]}),-1.0]])],"derivedFrom":subQ0})])]}),makeQuery(id+"F3.opExtrude","SWEPT_FACE",FACE,{"disambiguationData":[OSD([subQ0]),TDD([makeQuery(id+"F2.imprint","IMPRINT",EDGE,{"disambiguationData":[TD([[makeQuery(id+"F2.imprint","INTERSECT",VERTEX,{"derivedFrom":[sQuery(id+"F2.wireOp",EDGE,"E2.top"),subQ0]}),1.0]])],"derivedFrom":subQ0})])]}),makeQuery(id+"F4.opChamfer","BLEND_FACE",FACE,{"disambiguationData":[OSD([subQ2])]}),makeQuery(id+"F8.opExtrude","SWEPT_FACE",FACE,{"disambiguationData":[OSD([subQ2,subQ1,subQ3,subQ0])]}),makeQuery(id+"F8.opExtrude","SWEPT_FACE",FACE,{"disambiguationData":[OSD([subQ0])]}),makeQuery(id+"F10.opExtrude","SWEPT_FACE",FACE,{"disambiguationData":[OSD([sQuery(id+"F9.wireOp",EDGE,"E19")])]})])],"derivedFrom":makeQuery(id+"F8.boolean.opBoolean","MERGE",EDGE,{"derivedFrom":[makeQuery(id+"F4.opChamfer","BLEND_EDGE",EDGE,{"blendedFrom":[makeQuery(id+"F3.opExtrude","CAP_EDGE",EDGE,{"disambiguationData":[OSD([subQ2])],"isStart":false}),makeQuery(id+"F3.opExtrude","CAP_FACE",FACE,{"disambiguationData":[OSD([subQ2,subQ1,subQ3,subQ0])],"isStart":false})],"blendedInto":[makeQuery(id+"F3.opExtrude","CAP_FACE",FACE,{"disambiguationData":[OSD([subQ2,subQ1,subQ3,subQ0])],"isStart":false})]}),makeQuery(id+"F8.opExtrude","CAP_EDGE",EDGE,{"disambiguationData":[OSD([subQ2,subQ1,subQ3,subQ0])],"isStart":true})]})});}
            fillet(context, id + "F12", {"entities" : qUnion([Q0, Q1, Q2, Q3, Q4, Q5, Q6, Q7, Q8, Q9, Q10, Q11, Q12, Q13, Q14, Q15, Q16, Q17, Q18, Q19, Q20, Q21, Q22, Q23, Q24, Q25, Q26, Q27, Q28]), "radius" : 2 * mm, "tangentPropagation" : true, "allowEdgeOverflow" : false});
        }
        {
            var Q0;
            Q0=makeQuery(id+"F8.opExtrude","CAP_EDGE",EDGE,{"disambiguationData":[OSD([sQuery(id+"F2.wireOp",EDGE,"E1.bottom"),sQuery(id+"F2.wireOp",EDGE,"E2.bottom"),sQuery(id+"F2.wireOp",EDGE,"E2.left"),sQuery(id+"F2.wireOp",EDGE,"E2.right")])],"isStart":false});
            var Q1;
            {var subQ0=sQuery(id+"F2.wireOp",EDGE,"E2.left");var subQ1=sQuery(id+"F2.wireOp",EDGE,"E2.top");var subQ2=sQuery(id+"F2.wireOp",EDGE,"E1.top");var subQ3=makeQuery(id+"F3.opExtrude","CAP_FACE",FACE,{"disambiguationData":[OSD([subQ2,subQ1,subQ0,sQuery(id+"F2.wireOp",EDGE,"E2.right")])],"isStart":false});Q1=makeQuery(id+"F7.boolean.opBoolean","SPLIT",EDGE,{"disambiguationData":[TD([makeQuery(id+"F1.opExtrude","SWEPT_FACE",FACE,{"disambiguationData":[OSD([sQuery(id+"F0.wireOp",EDGE,"E0.left")])]})])],"derivedFrom":makeQuery(id+"F5.opChamfer","BLEND_EDGE",EDGE,{"blendedFrom":[makeQuery(id+"F3.opExtrude","CAP_EDGE",EDGE,{"disambiguationData":[OSD([subQ2])],"isStart":false}),subQ3],"blendedInto":[subQ3]})});}
            var Q2;
            {var subQ0=sQuery(id+"F2.wireOp",EDGE,"E2.top");Q2=makeQuery(id+"F7.boolean.opBoolean","SPLIT",EDGE,{"disambiguationData":[TD([makeQuery(id+"F1.opExtrude","SWEPT_FACE",FACE,{"disambiguationData":[OSD([sQuery(id+"F0.wireOp",EDGE,"E0.left")])]})])],"derivedFrom":makeQuery(id+"F3.opExtrude","CAP_EDGE",EDGE,{"disambiguationData":[OSD([subQ0])],"isStart":false})});}
            var Q3;
            {var subQ0=sQuery(id+"F2.wireOp",EDGE,"E2.top");var subQ1=sQuery(id+"F2.wireOp",EDGE,"E1.top");Q3=makeQuery(id+"F7.boolean.opBoolean","SPLIT",FACE,{"disambiguationData":[TD([makeQuery(id+"F7.opExtrude","SWEPT_FACE",FACE,{"disambiguationData":[OSD([sQuery(id+"F6.wireOp",EDGE,"E5")])]})])],"derivedFrom":makeQuery(id+"F3.opExtrude","CAP_FACE",FACE,{"disambiguationData":[OSD([subQ1,subQ0,sQuery(id+"F2.wireOp",EDGE,"E2.left"),sQuery(id+"F2.wireOp",EDGE,"E2.right")])],"isStart":false})});}
            var Q4;
            {var subQ0=sQuery(id+"F2.wireOp",EDGE,"E1.top");var subQ1=sQuery(id+"F2.wireOp",EDGE,"E2.top");Q4=makeQuery(id+"F7.boolean.opBoolean","SPLIT",FACE,{"disambiguationData":[TD([makeQuery(id+"F7.opExtrude","SWEPT_FACE",FACE,{"disambiguationData":[OSD([sQuery(id+"F6.wireOp",EDGE,"E9")])]})])],"derivedFrom":makeQuery(id+"F3.opExtrude","CAP_FACE",FACE,{"disambiguationData":[OSD([subQ0,subQ1,sQuery(id+"F2.wireOp",EDGE,"E2.left"),sQuery(id+"F2.wireOp",EDGE,"E2.right")])],"isStart":false})});}
            var Q5;
            {var subQ0=sQuery(id+"F2.wireOp",EDGE,"E1.top");var subQ1=sQuery(id+"F2.wireOp",EDGE,"E2.top");Q5=makeQuery(id+"F7.boolean.opBoolean","SPLIT",FACE,{"disambiguationData":[TD([makeQuery(id+"F7.opExtrude","SWEPT_FACE",FACE,{"disambiguationData":[OSD([sQuery(id+"F6.wireOp",EDGE,"E11")])]})])],"derivedFrom":makeQuery(id+"F3.opExtrude","CAP_FACE",FACE,{"disambiguationData":[OSD([subQ0,subQ1,sQuery(id+"F2.wireOp",EDGE,"E2.left"),sQuery(id+"F2.wireOp",EDGE,"E2.right")])],"isStart":false})});}
            var Q6;
            {var subQ0=sQuery(id+"F2.wireOp",EDGE,"E2.right");var subQ1=sQuery(id+"F2.wireOp",EDGE,"E2.top");var subQ2=sQuery(id+"F2.wireOp",EDGE,"E1.top");var subQ3=makeQuery(id+"F3.opExtrude","CAP_FACE",FACE,{"disambiguationData":[OSD([subQ2,subQ1,sQuery(id+"F2.wireOp",EDGE,"E2.left"),subQ0])],"isStart":false});Q6=makeQuery(id+"F7.boolean.opBoolean","SPLIT",EDGE,{"disambiguationData":[TD([makeQuery(id+"F1.opExtrude","SWEPT_FACE",FACE,{"disambiguationData":[OSD([sQuery(id+"F0.wireOp",EDGE,"E0.right")])]})])],"derivedFrom":makeQuery(id+"F5.opChamfer","BLEND_EDGE",EDGE,{"blendedFrom":[makeQuery(id+"F3.opExtrude","CAP_EDGE",EDGE,{"disambiguationData":[OSD([subQ2])],"isStart":false}),subQ3],"blendedInto":[subQ3]})});}
            var Q7;
            {var subQ0=sQuery(id+"F2.wireOp",EDGE,"E2.top");Q7=makeQuery(id+"F7.boolean.opBoolean","SPLIT",EDGE,{"disambiguationData":[TD([makeQuery(id+"F1.opExtrude","SWEPT_FACE",FACE,{"disambiguationData":[OSD([sQuery(id+"F0.wireOp",EDGE,"E0.right")])]})])],"derivedFrom":makeQuery(id+"F3.opExtrude","CAP_EDGE",EDGE,{"disambiguationData":[OSD([subQ0])],"isStart":false})});}
            fillet(context, id + "F13", {"entities" : qUnion([Q0, Q1, Q2, Q3, Q4, Q5, Q6, Q7]), "radius" : 3 * mm, "tangentPropagation" : true, "allowEdgeOverflow" : false});
        }
    });
